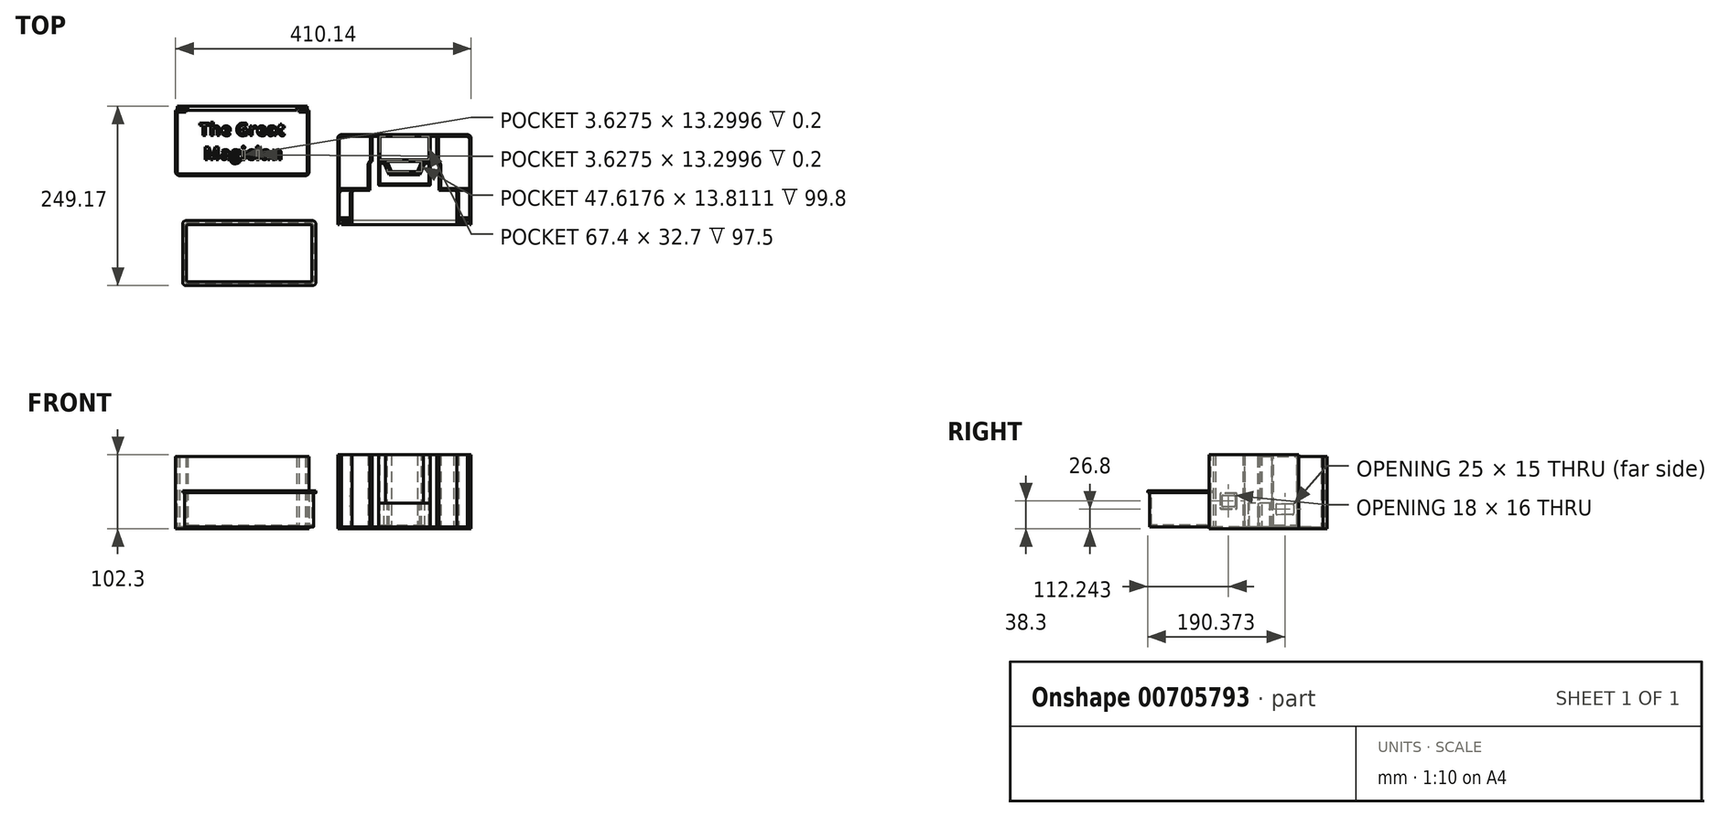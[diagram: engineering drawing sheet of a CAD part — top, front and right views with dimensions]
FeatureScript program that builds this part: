
annotation { "Feature Type Name" : "Feature", "Feature Type Description" : "" }
export const myFeature = defineFeature(function(context is Context, id is Id, definition is map)
    precondition{}
    {
        {
            var Q0;
            Q0=qCreatedBy(makeId("Top.planeOp"),FACE);
            var sketch = newSketch(context, id + "F0", { "sketchPlane" : qUnion([Q0])});
            skLineSegment(sketch, "E0.top", {"start": v(-1, -57.37) * mm, "end": v(-73, -57.37) * mm});
            skLineSegment(sketch, "E0.right", {"start": v(-73, -12.37) * mm, "end": v(-73, -57.37) * mm});
            skLineSegment(sketch, "E1.right", {"start": v(-84, -57.37) * mm, "end": v(-84, -57.37) * mm});
            skLineSegment(sketch, "E2.top", {"start": v(0, 62.63) * mm, "end": v(-45, 62.63) * mm});
            skLineSegment(sketch, "E2.right", {"start": v(-45, 27.63) * mm, "end": v(-45, 62.63) * mm});
            skLineSegment(sketch, "E3.MirrorCS", {"start": v(45, 27.63) * mm, "end": v(45, 62.63) * mm});
            skLineSegment(sketch, "E4.MirrorCS", {"start": v(0, 62.63) * mm, "end": v(45, 62.63) * mm});
            skLineSegment(sketch, "E5.MirrorCS", {"start": v(73, -12.37) * mm, "end": v(73, -57.37) * mm});
            skLineSegment(sketch, "E6.MirrorCS", {"start": v(-1, -57.37) * mm, "end": v(73, -57.37) * mm});
            skLineSegment(sketch, "E7", {"start": v(-36, 62.63) * mm, "end": v(-36, 27.63) * mm});
            skLineSegment(sketch, "E8.MirrorCS", {"start": v(36, 73.63) * mm, "end": v(36, 27.63) * mm});
            skLineSegment(sketch, "E9.trimOffspring", {"start": v(-48, -12.37) * mm, "end": v(-73, -12.37) * mm});
            skPoint(sketch, "E10.orphan", {"position": v(40, -12.37) * mm});
            skLineSegment(sketch, "E11.trimOffspring", {"start": v(48, -12.37) * mm, "end": v(73, -12.37) * mm});
            skPoint(sketch, "E12.orphan", {"position": v(73, -57.37) * mm});
            skPoint(sketch, "E13.orphan", {"position": v(0, 62.63) * mm});
            skLineSegment(sketch, "E14.bottom", {"start": v(-304.84, -57.37) * mm, "end": v(-125.84, -57.37) * mm});
            skLineSegment(sketch, "E14.top", {"start": v(-304.84, -141.67) * mm, "end": v(-125.84, -141.67) * mm});
            skLineSegment(sketch, "E14.left", {"start": v(-304.84, -57.37) * mm, "end": v(-304.84, -141.67) * mm});
            skLineSegment(sketch, "E14.right", {"start": v(-125.84, -57.37) * mm, "end": v(-125.84, -141.67) * mm});
            skLineSegment(sketch, "E15.0", {"start": v(-307.84, -54.37) * mm, "end": v(-122.84, -54.37) * mm});
            skLineSegment(sketch, "E15.1", {"start": v(-307.84, -54.37) * mm, "end": v(-307.84, -144.67) * mm});
            skLineSegment(sketch, "E15.2", {"start": v(-307.84, -144.67) * mm, "end": v(-122.84, -144.67) * mm});
            skLineSegment(sketch, "E15.3", {"start": v(-122.84, -54.37) * mm, "end": v(-122.84, -144.67) * mm});
            skLineSegment(sketch, "E16", {"start": v(-36, 27.63) * mm, "end": v(36, 27.63) * mm});
            skLineSegment(sketch, "E17", {"start": v(-45, 27.63) * mm, "end": v(-48, 27.63) * mm});
            skLineSegment(sketch, "E18", {"start": v(-48, 27.63) * mm, "end": v(-48, -12.37) * mm});
            skLineSegment(sketch, "E19", {"start": v(0, 62.63) * mm, "end": v(0, 0) * mm, "construction": true});
            skLineSegment(sketch, "E20.MirrorCS", {"start": v(45, 27.63) * mm, "end": v(48, 27.63) * mm});
            skLineSegment(sketch, "E21.MirrorCS", {"start": v(48, 27.63) * mm, "end": v(48, -12.37) * mm});
            skLineSegment(sketch, "E22", {"start": v(-36, 27.63) * mm, "end": v(-26.5, 27.63) * mm});
            skLineSegment(sketch, "E23", {"start": v(-26.5, 27.63) * mm, "end": v(-20, 11.32) * mm});
            skLineSegment(sketch, "E24", {"start": v(-20, 11.32) * mm, "end": v(0, 11.32) * mm});
            skLineSegment(sketch, "E25.MirrorCS", {"start": v(20, 11.32) * mm, "end": v(0, 11.32) * mm});
            skLineSegment(sketch, "E26.MirrorCS", {"start": v(26.5, 27.63) * mm, "end": v(20, 11.32) * mm});
            skLineSegment(sketch, "E27.MirrorCS", {"start": v(36, 27.63) * mm, "end": v(26.5, 27.63) * mm});
            skPoint(sketch, "E28.MirrorCS.end.orphan", {"position": v(36, -18.37) * mm});
            skPoint(sketch, "E0.bottom.end.orphan", {"position": v(-36, -7.37) * mm});
            skLineSegment(sketch, "E29", {"start": v(-36, 27.63) * mm, "end": v(-36, -5.6) * mm});
            skLineSegment(sketch, "E30", {"start": v(-36, -5.6) * mm, "end": v(36, -5.6) * mm});
            skLineSegment(sketch, "E31", {"start": v(36, 27.63) * mm, "end": v(36, -5.6) * mm});
            skLineSegment(sketch, "E32.top", {"start": v(-303.24, 96.2) * mm, "end": v(-315.24, 96.2) * mm});
            skLineSegment(sketch, "E32.right", {"start": v(-315.24, 10.5) * mm, "end": v(-315.24, 96.2) * mm});
            skLineSegment(sketch, "E33.MirrorCS", {"start": v(-134.64, 10.5) * mm, "end": v(-134.64, 96.2) * mm});
            skPoint(sketch, "E34.MirrorCS.end.orphan", {"position": v(84, -57.37) * mm});
            skPoint(sketch, "E35.MirrorCS.end.orphan", {"position": v(84, -57.73) * mm});
            skLineSegment(sketch, "E36.1", {"start": v(-132.34, 8.2) * mm, "end": v(-132.34, 98.5) * mm});
            skLineSegment(sketch, "E36.4", {"start": v(-303.24, 98.5) * mm, "end": v(-312.34, 98.5) * mm});
            skLineSegment(sketch, "E36.5", {"start": v(-317.54, 8.2) * mm, "end": v(-317.54, 98.5) * mm});
            skLineSegment(sketch, "E37", {"start": v(-303.24, 96.2) * mm, "end": v(-303.24, 98.5) * mm});
            skLineSegment(sketch, "E38.top", {"start": v(-315.04, 104.5) * mm, "end": v(-312.34, 104.5) * mm});
            skLineSegment(sketch, "E38.right", {"start": v(-312.34, 98.5) * mm, "end": v(-312.34, 101.8) * mm});
            skLineSegment(sketch, "E39.bottom", {"start": v(-312.34, 104.5) * mm, "end": v(-300.54, 104.5) * mm});
            skLineSegment(sketch, "E39.top", {"start": v(-312.34, 101.8) * mm, "end": v(-300.54, 101.8) * mm});
            skLineSegment(sketch, "E39.right", {"start": v(-300.54, 104.5) * mm, "end": v(-300.54, 101.8) * mm});
            skLineSegment(sketch, "E40.trimOffspring", {"start": v(-315.24, 98.5) * mm, "end": v(-317.54, 98.5) * mm});
            skLineSegment(sketch, "E41", {"start": v(-315.24, 10.5) * mm, "end": v(-134.64, 10.5) * mm});
            skLineSegment(sketch, "E42", {"start": v(-317.54, 8.2) * mm, "end": v(-132.34, 8.2) * mm});
            skLineSegment(sketch, "E43", {"start": v(-224.94, 10.5) * mm, "end": v(-224.94, 18.93) * mm, "construction": true});
            skLineSegment(sketch, "E44.MirrorCS", {"start": v(-137.54, 98.5) * mm, "end": v(-137.54, 101.8) * mm});
            skLineSegment(sketch, "E45.MirrorCS", {"start": v(-137.54, 104.5) * mm, "end": v(-149.34, 104.5) * mm});
            skLineSegment(sketch, "E46.MirrorCS", {"start": v(-137.54, 101.8) * mm, "end": v(-149.34, 101.8) * mm});
            skLineSegment(sketch, "E47.MirrorCS", {"start": v(-149.34, 104.5) * mm, "end": v(-149.34, 101.8) * mm});
            skLineSegment(sketch, "E48.MirrorCS", {"start": v(-146.64, 98.5) * mm, "end": v(-137.54, 98.5) * mm});
            skLineSegment(sketch, "E49.MirrorCS", {"start": v(-146.64, 96.2) * mm, "end": v(-146.64, 98.5) * mm});
            skLineSegment(sketch, "E50.MirrorCS", {"start": v(-146.64, 96.2) * mm, "end": v(-134.64, 96.2) * mm});
            skLineSegment(sketch, "E51.MirrorCS", {"start": v(-134.64, 98.5) * mm, "end": v(-132.34, 98.5) * mm});
            skLineSegment(sketch, "E52", {"start": v(-315.24, 98.5) * mm, "end": v(-315.04, 98.5) * mm});
            skLineSegment(sketch, "E53", {"start": v(-315.04, 98.5) * mm, "end": v(-315.04, 104.5) * mm});
            skPoint(sketch, "E54.orphan", {"position": v(-315.24, 104.5) * mm});
            skLineSegment(sketch, "E55.MirrorCS", {"start": v(-134.84, 98.5) * mm, "end": v(-134.84, 104.5) * mm});
            skLineSegment(sketch, "E56.MirrorCS", {"start": v(-134.84, 104.5) * mm, "end": v(-137.54, 104.5) * mm});
            skLineSegment(sketch, "E57.MirrorCS", {"start": v(-134.64, 98.5) * mm, "end": v(-134.84, 98.5) * mm});
            skSolve(sketch);
        }
        {
            var Q0;
            Q0=makeQuery(id+"F0.imprint","IMPRINT",FACE,{"disambiguationData":[TD([[makeQuery(id+"F0.imprint","IMPRINT",EDGE,{"derivedFrom":sQuery(id+"F0.wireOp",EDGE,"E0.top")}),-1.0]])]});
            var Q1;
            {var subQ4=sQuery(id+"F0.wireOp",EDGE,"E0.left");Q1=makeQuery(id+"F0.imprint","IMPRINT",FACE,{"disambiguationData":[TD([[makeQuery(id+"F0.imprint","IMPRINT",EDGE,{"derivedFrom":subQ4}),1.0]])]});}
            var Q2;
            Q2=makeQuery(id+"F0.imprint","IMPRINT",FACE,{"disambiguationData":[TD([[makeQuery(id+"F0.imprint","IMPRINT",EDGE,{"derivedFrom":sQuery(id+"F0.wireOp",EDGE,"E0.bottom")}),1.0]])]});
            var Q3;
            Q3=makeQuery(id+"F0.imprint","IMPRINT",FACE,{"disambiguationData":[TD([[makeQuery(id+"F0.imprint","IMPRINT",EDGE,{"derivedFrom":sQuery(id+"F0.wireOp",EDGE,"E1.bottom")}),-1.0]])]});
            var Q4;
            {var subQ2=sQuery(id+"F0.wireOp",EDGE,"E35.MirrorCS");Q4=makeQuery(id+"F0.imprint","IMPRINT",FACE,{"disambiguationData":[TD([[makeQuery(id+"F0.imprint","IMPRINT",EDGE,{"derivedFrom":subQ2}),-1.0]])]});}
            var Q5;
            Q5=makeQuery(id+"F0.imprint","IMPRINT",FACE,{"disambiguationData":[TD([[makeQuery(id+"F0.imprint","IMPRINT",EDGE,{"derivedFrom":sQuery(id+"F0.wireOp",EDGE,"E2.bottom")}),-1.0]])]});
            var Q6;
            {var subQ0=sQuery(id+"F0.wireOp",EDGE,"E7");Q6=makeQuery(id+"F0.imprint","IMPRINT",FACE,{"disambiguationData":[TD([[makeQuery(id+"F0.imprint","IMPRINT",EDGE,{"derivedFrom":subQ0}),1.0]])]});}
            var Q7;
            {var subQ0=sQuery(id+"F0.wireOp",EDGE,"E23");Q7=makeQuery(id+"F0.imprint","IMPRINT",FACE,{"disambiguationData":[TD([[makeQuery(id+"F0.imprint","IMPRINT",EDGE,{"derivedFrom":subQ0}),1.0]])]});}
            var Q8;
            {var subQ0=sQuery(id+"F0.wireOp",EDGE,"E23");Q8=makeQuery(id+"F0.imprint","IMPRINT",FACE,{"disambiguationData":[TD([[makeQuery(id+"F0.imprint","IMPRINT",EDGE,{"derivedFrom":subQ0}),-1.0]])]});}
            var Q9;
            Q9=makeQuery(id+"F0.imprint","IMPRINT",FACE,{"disambiguationData":[TD([[makeQuery(id+"F0.imprint","IMPRINT",EDGE,{"derivedFrom":sQuery(id+"F0.wireOp",EDGE,"c8318e10-518c-48d9-a7b7-4d28b4569db7.top")}),1.0]])]});
            extrude(context, id + "F1", {"entities" : qUnion([Q0, Q1, Q2, Q3, Q4, Q5, Q6, Q7, Q8, Q9]), "depth" : 100 * mm, "offsetDistance" : 25 * mm});
        }
        {
            var Q0;
            Q0=makeQuery(id+"F0.imprint","IMPRINT",FACE,{"disambiguationData":[TD([[makeQuery(id+"F0.imprint","IMPRINT",EDGE,{"derivedFrom":sQuery(id+"F0.wireOp",EDGE,"E32.top")}),-1.0]])]});
            extrude(context, id + "F2", {"entities" : qUnion([Q0]), "depth" : 97.5 * mm, "offsetDistance" : 25 * mm});
        }
        {
            var Q0;
            Q0=makeQuery(id+"F1.opExtrude","SWEPT_EDGE",EDGE,{"disambiguationData":[OSD([sQuery(id+"F0.wireOp",EDGE,"E0.right"),sQuery(id+"F0.wireOp",EDGE,"E9.trimOffspring")])]});
            var Q1;
            Q1=makeQuery(id+"F1.opExtrude","SWEPT_EDGE",EDGE,{"disambiguationData":[OSD([sQuery(id+"F0.wireOp",EDGE,"E17"),sQuery(id+"F0.wireOp",EDGE,"E18")])]});
            var Q2;
            Q2=makeQuery(id+"F1.opExtrude","SWEPT_EDGE",EDGE,{"disambiguationData":[OSD([sQuery(id+"F0.wireOp",EDGE,"E20.MirrorCS"),sQuery(id+"F0.wireOp",EDGE,"E21.MirrorCS")])]});
            var Q3;
            Q3=makeQuery(id+"F1.opExtrude","SWEPT_EDGE",EDGE,{"disambiguationData":[OSD([sQuery(id+"F0.wireOp",EDGE,"E5.MirrorCS"),sQuery(id+"F0.wireOp",EDGE,"E11.trimOffspring")])]});
            fillet(context, id + "F3", {"entities" : qUnion([Q0, Q1, Q2, Q3]), "radius" : 5 * mm, "tangentPropagation" : true, "allowEdgeOverflow" : false});
        }
        {
            var Q0;
            Q0=makeQuery(id+"F1.opExtrude","CAP_FACE",FACE,{"disambiguationData":[OSD([sQuery(id+"F0.wireOp",EDGE,"E0.top"),sQuery(id+"F0.wireOp",EDGE,"E0.right"),sQuery(id+"F0.wireOp",EDGE,"E2.top"),sQuery(id+"F0.wireOp",EDGE,"E2.right"),sQuery(id+"F0.wireOp",EDGE,"E3.MirrorCS"),sQuery(id+"F0.wireOp",EDGE,"E4.MirrorCS"),sQuery(id+"F0.wireOp",EDGE,"E5.MirrorCS"),sQuery(id+"F0.wireOp",EDGE,"E6.MirrorCS"),sQuery(id+"F0.wireOp",EDGE,"E9.trimOffspring"),sQuery(id+"F0.wireOp",EDGE,"E11.trimOffspring"),sQuery(id+"F0.wireOp",EDGE,"E17"),sQuery(id+"F0.wireOp",EDGE,"E18"),sQuery(id+"F0.wireOp",EDGE,"E20.MirrorCS"),sQuery(id+"F0.wireOp",EDGE,"E21.MirrorCS")])],"isStart":false});
            shell(context, id + "F4", {"entities" : qUnion([Q0]), "thickness" : 2.3 * mm, "oppositeDirection" : true});
        }
        {
            var Q0;
            {var subQ0=sQuery(id+"F0.wireOp",EDGE,"E7");Q0=makeQuery(id+"F0.imprint","IMPRINT",FACE,{"disambiguationData":[TD([[makeQuery(id+"F0.imprint","IMPRINT",EDGE,{"derivedFrom":subQ0}),1.0]])]});}
            var Q1;
            {var subQ4=sQuery(id+"F0.wireOp",EDGE,"E2.bottom");Q1=makeQuery(id+"F0.imprint","IMPRINT",FACE,{"disambiguationData":[TD([[makeQuery(id+"F0.imprint","IMPRINT",EDGE,{"derivedFrom":subQ4}),-1.0]])]});}
            var Q2;
            {var subQ0=sQuery(id+"F0.wireOp",EDGE,"E23");Q2=makeQuery(id+"F0.imprint","IMPRINT",FACE,{"disambiguationData":[TD([[makeQuery(id+"F0.imprint","IMPRINT",EDGE,{"derivedFrom":subQ0}),1.0]])]});}
            extrude(context, id + "F5", {"entities" : qUnion([Q0, Q1, Q2]), "operationType" : NewBodyOperationType.ADD, "depth" : 100 * mm, "offsetDistance" : 25 * mm});
        }
        {
            var Q0;
            {var subQ0=sQuery(id+"F0.wireOp",EDGE,"E4.MirrorCS");var subQ1=sQuery(id+"F0.wireOp",EDGE,"E2.top");Q0=makeQuery(id+"F5.boolean.opBoolean","MERGE",FACE,{"derivedFrom":[makeQuery(id+"F1.opExtrude","CAP_FACE",FACE,{"disambiguationData":[OSD([sQuery(id+"F0.wireOp",EDGE,"E0.top"),sQuery(id+"F0.wireOp",EDGE,"E0.right"),subQ1,sQuery(id+"F0.wireOp",EDGE,"E2.right"),sQuery(id+"F0.wireOp",EDGE,"E3.MirrorCS"),subQ0,sQuery(id+"F0.wireOp",EDGE,"E5.MirrorCS"),sQuery(id+"F0.wireOp",EDGE,"E6.MirrorCS"),sQuery(id+"F0.wireOp",EDGE,"E9.trimOffspring"),sQuery(id+"F0.wireOp",EDGE,"E11.trimOffspring"),sQuery(id+"F0.wireOp",EDGE,"E17"),sQuery(id+"F0.wireOp",EDGE,"E18"),sQuery(id+"F0.wireOp",EDGE,"E20.MirrorCS"),sQuery(id+"F0.wireOp",EDGE,"E21.MirrorCS")])],"isStart":false}),makeQuery(id+"F5.opExtrude","CAP_FACE",FACE,{"disambiguationData":[OSD([subQ1,subQ0,sQuery(id+"F0.wireOp",EDGE,"E7"),sQuery(id+"F0.wireOp",EDGE,"E8.MirrorCS"),sQuery(id+"F0.wireOp",EDGE,"E16"),sQuery(id+"F0.wireOp",EDGE,"E23"),sQuery(id+"F0.wireOp",EDGE,"E24"),sQuery(id+"F0.wireOp",EDGE,"E25.MirrorCS"),sQuery(id+"F0.wireOp",EDGE,"E26.MirrorCS")])],"isStart":false})]});}
            shell(context, id + "F6", {"entities" : qUnion([Q0]), "thickness" : 2.5 * mm});
        }
        {
            var Q0;
            {var subQ0=sQuery(id+"F0.wireOp",EDGE,"E23");Q0=makeQuery(id+"F0.imprint","IMPRINT",FACE,{"disambiguationData":[TD([[makeQuery(id+"F0.imprint","IMPRINT",EDGE,{"derivedFrom":subQ0}),-1.0]])]});}
            extrude(context, id + "F7", {"entities" : qUnion([Q0]), "operationType" : NewBodyOperationType.ADD, "depth" : 33 * mm, "offsetDistance" : 25 * mm});
        }
        {
            var Q0;
            Q0=makeQuery(id+"F0.imprint","IMPRINT",FACE,{"disambiguationData":[TD([[makeQuery(id+"F0.imprint","IMPRINT",EDGE,{"derivedFrom":sQuery(id+"F0.wireOp",EDGE,"E14.bottom")}),-1.0]])]});
            var Q1;
            Q1=makeQuery(id+"F0.imprint","IMPRINT",FACE,{"disambiguationData":[TD([[makeQuery(id+"F0.imprint","IMPRINT",EDGE,{"derivedFrom":sQuery(id+"F0.wireOp",EDGE,"E14.bottom")}),1.0]])]});
            extrude(context, id + "F8", {"entities" : qUnion([Q0, Q1]), "depth" : 50 * mm, "offsetDistance" : 25 * mm});
        }
        {
            var Q0;
            Q0=makeQuery(id+"F0.imprint","IMPRINT",FACE,{"disambiguationData":[TD([[makeQuery(id+"F0.imprint","IMPRINT",EDGE,{"derivedFrom":sQuery(id+"F0.wireOp",EDGE,"E14.bottom")}),1.0]])]});
            extrude(context, id + "F9", {"entities" : qUnion([Q0]), "operationType" : NewBodyOperationType.REMOVE, "depth" : 47.5 * mm, "offsetDistance" : 25 * mm});
        }
        {
            var Q0;
            Q0=makeQuery(id+"F9.boolean.opBoolean","COPY",EDGE,{"derivedFrom":makeQuery(id+"F9.opExtrude","SWEPT_EDGE",EDGE,{"disambiguationData":[OSD([sQuery(id+"F0.wireOp",EDGE,"E14.top"),sQuery(id+"F0.wireOp",EDGE,"E14.left")])]})});
            var Q1;
            Q1=makeQuery(id+"F9.boolean.opBoolean","COPY",EDGE,{"derivedFrom":makeQuery(id+"F9.opExtrude","SWEPT_EDGE",EDGE,{"disambiguationData":[OSD([sQuery(id+"F0.wireOp",EDGE,"E14.bottom"),sQuery(id+"F0.wireOp",EDGE,"E14.left")])]})});
            var Q2;
            Q2=makeQuery(id+"F8.opExtrude","SWEPT_EDGE",EDGE,{"disambiguationData":[OSD([sQuery(id+"F0.wireOp",EDGE,"E15.1"),sQuery(id+"F0.wireOp",EDGE,"E15.2")])]});
            var Q3;
            Q3=makeQuery(id+"F8.opExtrude","SWEPT_EDGE",EDGE,{"disambiguationData":[OSD([sQuery(id+"F0.wireOp",EDGE,"E15.0"),sQuery(id+"F0.wireOp",EDGE,"E15.1")])]});
            var Q4;
            Q4=makeQuery(id+"F8.opExtrude","SWEPT_EDGE",EDGE,{"disambiguationData":[OSD([sQuery(id+"F0.wireOp",EDGE,"E15.0"),sQuery(id+"F0.wireOp",EDGE,"E15.3")])]});
            var Q5;
            Q5=makeQuery(id+"F9.boolean.opBoolean","COPY",EDGE,{"derivedFrom":makeQuery(id+"F9.opExtrude","SWEPT_EDGE",EDGE,{"disambiguationData":[OSD([sQuery(id+"F0.wireOp",EDGE,"E14.bottom"),sQuery(id+"F0.wireOp",EDGE,"E14.right")])]})});
            var Q6;
            Q6=makeQuery(id+"F8.opExtrude","SWEPT_EDGE",EDGE,{"disambiguationData":[OSD([sQuery(id+"F0.wireOp",EDGE,"E15.2"),sQuery(id+"F0.wireOp",EDGE,"E15.3")])]});
            var Q7;
            Q7=makeQuery(id+"F9.boolean.opBoolean","COPY",EDGE,{"derivedFrom":makeQuery(id+"F9.opExtrude","SWEPT_EDGE",EDGE,{"disambiguationData":[OSD([sQuery(id+"F0.wireOp",EDGE,"E14.top"),sQuery(id+"F0.wireOp",EDGE,"E14.right")])]})});
            fillet(context, id + "F10", {"entities" : qUnion([Q0, Q1, Q2, Q3, Q4, Q5, Q6, Q7]), "radius" : 5 * mm, "tangentPropagation" : true, "allowEdgeOverflow" : false});
        }
        {
            var Q0;
            Q0=makeQuery(id+"F8.opExtrude","CAP_FACE",FACE,{"disambiguationData":[OSD([sQuery(id+"F0.wireOp",EDGE,"E15.0"),sQuery(id+"F0.wireOp",EDGE,"E15.1"),sQuery(id+"F0.wireOp",EDGE,"E15.2"),sQuery(id+"F0.wireOp",EDGE,"E15.3")])],"isStart":false});
            shell(context, id + "F11", {"entities" : qUnion([Q0]), "thickness" : 2.5 * mm});
        }
        {
            var Q0;
            Q0=makeQuery(id+"F1.opExtrude","SWEPT_EDGE",EDGE,{"disambiguationData":[OSD([sQuery(id+"F0.wireOp",EDGE,"E0.top"),sQuery(id+"F0.wireOp",EDGE,"E0.right")])]});
            var Q1;
            Q1=makeQuery(id+"F1.opExtrude","SWEPT_EDGE",EDGE,{"disambiguationData":[OSD([sQuery(id+"F0.wireOp",EDGE,"E5.MirrorCS"),sQuery(id+"F0.wireOp",EDGE,"E6.MirrorCS")])]});
            var Q2;
            Q2=makeQuery(id+"F1.opExtrude","SWEPT_EDGE",EDGE,{"disambiguationData":[OSD([sQuery(id+"F0.wireOp",EDGE,"E9.trimOffspring"),sQuery(id+"F0.wireOp",EDGE,"E18")])]});
            var Q3;
            Q3=makeQuery(id+"F1.opExtrude","SWEPT_EDGE",EDGE,{"disambiguationData":[OSD([sQuery(id+"F0.wireOp",EDGE,"E11.trimOffspring"),sQuery(id+"F0.wireOp",EDGE,"E21.MirrorCS")])]});
            fillet(context, id + "F12", {"entities" : qUnion([Q0, Q1, Q2, Q3]), "radius" : 1 * mm, "tangentPropagation" : true, "allowEdgeOverflow" : false});
        }
        {
            var Q0;
            {var subQ0=sQuery(id+"F0.wireOp",EDGE,"E7");Q0=makeQuery(id+"F0.imprint","IMPRINT",FACE,{"disambiguationData":[TD([[makeQuery(id+"F0.imprint","IMPRINT",EDGE,{"derivedFrom":subQ0}),1.0]])]});}
            extrude(context, id + "F13", {"entities" : qUnion([Q0]), "operationType" : NewBodyOperationType.ADD, "depth" : 100 * mm, "offsetDistance" : 25 * mm});
        }
        {
            var Q0;
            {var subQ0=sQuery(id+"F0.wireOp",EDGE,"E16");var subQ1=sQuery(id+"F0.wireOp",EDGE,"E8.MirrorCS");var subQ2=sQuery(id+"F0.wireOp",EDGE,"E7");var subQ3=sQuery(id+"F0.wireOp",EDGE,"E4.MirrorCS");var subQ4=sQuery(id+"F0.wireOp",EDGE,"E2.top");Q0=makeQuery(id+"F13.boolean.opBoolean","MERGE",FACE,{"derivedFrom":[makeQuery(id+"F5.boolean.opBoolean","MERGE",FACE,{"derivedFrom":[makeQuery(id+"F1.opExtrude","CAP_FACE",FACE,{"disambiguationData":[OSD([sQuery(id+"F0.wireOp",EDGE,"E0.top"),sQuery(id+"F0.wireOp",EDGE,"E0.right"),subQ4,sQuery(id+"F0.wireOp",EDGE,"E2.right"),sQuery(id+"F0.wireOp",EDGE,"E3.MirrorCS"),subQ3,sQuery(id+"F0.wireOp",EDGE,"E5.MirrorCS"),sQuery(id+"F0.wireOp",EDGE,"E6.MirrorCS"),sQuery(id+"F0.wireOp",EDGE,"E9.trimOffspring"),sQuery(id+"F0.wireOp",EDGE,"E11.trimOffspring"),sQuery(id+"F0.wireOp",EDGE,"E17"),sQuery(id+"F0.wireOp",EDGE,"E18"),sQuery(id+"F0.wireOp",EDGE,"E20.MirrorCS"),sQuery(id+"F0.wireOp",EDGE,"E21.MirrorCS")])],"isStart":false}),makeQuery(id+"F5.opExtrude","CAP_FACE",FACE,{"disambiguationData":[OSD([subQ4,subQ3,subQ2,subQ1,subQ0,sQuery(id+"F0.wireOp",EDGE,"E23"),sQuery(id+"F0.wireOp",EDGE,"E24"),sQuery(id+"F0.wireOp",EDGE,"E25.MirrorCS"),sQuery(id+"F0.wireOp",EDGE,"E26.MirrorCS")])],"isStart":false})]}),makeQuery(id+"F13.opExtrude","CAP_FACE",FACE,{"disambiguationData":[OSD([subQ4,subQ3,subQ2,subQ1,subQ0])],"isStart":false})]});}
            var sketch = newSketch(context, id + "F14", { "sketchPlane" : qUnion([Q0])});
            skPoint(sketch, "E58.oppositeSnap0", {"position": v(40.5, 62.63) * mm});
            skLineSegment(sketch, "E59.bottom", {"start": v(-33.7, 29.93) * mm, "end": v(33.7, 29.93) * mm});
            skLineSegment(sketch, "E59.top", {"start": v(-33.7, 62.63) * mm, "end": v(33.7, 62.63) * mm});
            skLineSegment(sketch, "E59.left", {"start": v(-33.7, 29.93) * mm, "end": v(-33.7, 62.63) * mm});
            skLineSegment(sketch, "E59.right", {"start": v(33.7, 29.93) * mm, "end": v(33.7, 62.63) * mm});
            skSolve(sketch);
        }
        {
            var Q0;
            Q0=makeQuery(id+"F14.imprint","IMPRINT",FACE,{"disambiguationData":[TD([[makeQuery(id+"F14.imprint","IMPRINT",EDGE,{"derivedFrom":sQuery(id+"F14.wireOp",EDGE,"E59.bottom")}),1.0]])]});
            extrude(context, id + "F15", {"entities" : qUnion([Q0]), "operationType" : NewBodyOperationType.REMOVE, "oppositeDirection" : true, "depth" : 97.5 * mm, "offsetDistance" : 25 * mm});
        }
        {
            var Q0;
            Q0=makeQuery(id+"F14.imprint","IMPRINT",FACE,{"disambiguationData":[TD([[makeQuery(id+"F14.imprint","IMPRINT",EDGE,{"derivedFrom":sQuery(id+"F14.wireOp",EDGE,"E59.bottom")}),-1.0]])]});
            var sketch = newSketch(context, id + "F16", { "sketchPlane" : qUnion([Q0])});
            skLineSegment(sketch, "E60.bottom", {"start": v(-73, -57.37) * mm, "end": v(73, -57.37) * mm});
            skLineSegment(sketch, "E60.top", {"start": v(-73, -59.67) * mm, "end": v(73, -59.67) * mm});
            skLineSegment(sketch, "E60.left", {"start": v(-73, -57.37) * mm, "end": v(-73, -59.67) * mm});
            skLineSegment(sketch, "E60.right", {"start": v(73, -57.37) * mm, "end": v(73, -59.67) * mm});
            skLineSegment(sketch, "E61.bottom", {"start": v(-72.99, -56.77) * mm, "end": v(-87.2, -56.77) * mm});
            skLineSegment(sketch, "E61.top", {"start": v(-72, -59.67) * mm, "end": v(-87.2, -59.67) * mm});
            skLineSegment(sketch, "E61.right", {"start": v(-87.2, -56.77) * mm, "end": v(-87.2, -59.67) * mm});
            skLineSegment(sketch, "E62.top", {"start": v(74, -59.67) * mm, "end": v(87.2, -59.67) * mm});
            skPoint(sketch, "E63", {"position": v(-72.99, -56.77) * mm});
            skLineSegment(sketch, "E64", {"start": v(0, -57.37) * mm, "end": v(0, -53.18) * mm, "construction": true});
            skLineSegment(sketch, "E65.MirrorCS", {"start": v(72.99, -56.77) * mm, "end": v(87.2, -56.77) * mm});
            skLineSegment(sketch, "E66.MirrorCS", {"start": v(87.2, -56.77) * mm, "end": v(87.2, -59.67) * mm});
            skLineSegment(sketch, "E67.MirrorCS", {"start": v(72, -59.67) * mm, "end": v(87.2, -59.67) * mm});
            skSolve(sketch);
        }
        {
            var Q0;
            Q0=makeQuery(id+"F16.imprint","IMPRINT",FACE,{"disambiguationData":[TD([[makeQuery(id+"F16.imprint","IMPRINT",EDGE,{"derivedFrom":sQuery(id+"F16.wireOp",EDGE,"E60.bottom")}),1.0]])]});
            extrude(context, id + "F17", {"entities" : qUnion([Q0]), "operationType" : NewBodyOperationType.REMOVE, "oppositeDirection" : true, "depth" : 100 * mm, "offsetDistance" : 25 * mm});
        }
        {
            var Q0;
            {var subQ0=sQuery(id+"F16.wireOp",EDGE,"E61.right");Q0=makeQuery(id+"F16.imprint","IMPRINT",FACE,{"disambiguationData":[TD([[makeQuery(id+"F16.imprint","IMPRINT",EDGE,{"derivedFrom":subQ0}),1.0]])]});}
            var Q1;
            {var subQ0=sQuery(id+"F16.wireOp",EDGE,"E62.right");Q1=makeQuery(id+"F16.imprint","IMPRINT",FACE,{"disambiguationData":[TD([[makeQuery(id+"F16.imprint","IMPRINT",EDGE,{"derivedFrom":subQ0}),-1.0]])]});}
            var Q2;
            {var subQ6=sQuery(id+"F16.wireOp",EDGE,"E66.MirrorCS");Q2=makeQuery(id+"F16.imprint","IMPRINT",FACE,{"disambiguationData":[TD([[makeQuery(id+"F16.imprint","IMPRINT",EDGE,{"derivedFrom":subQ6}),-1.0]])]});}
            extrude(context, id + "F18", {"entities" : qUnion([Q0, Q1, Q2]), "operationType" : NewBodyOperationType.ADD, "oppositeDirection" : true, "depth" : 100 * mm, "offsetDistance" : 25 * mm});
        }
        {
            var Q0;
            Q0=makeQuery(id+"F2.opExtrude","SWEPT_FACE",FACE,{"disambiguationData":[OSD([sQuery(id+"F0.wireOp",EDGE,"E36.5")])]});
            var sketch = newSketch(context, id + "F19", { "sketchPlane" : qUnion([Q0])});
            skLineSegment(sketch, "E68.bottom", {"start": v(-58.2, 32) * mm, "end": v(-33.2, 32) * mm});
            skLineSegment(sketch, "E68.top", {"start": v(-58.2, 17) * mm, "end": v(-33.2, 17) * mm});
            skLineSegment(sketch, "E68.left", {"start": v(-58.2, 32) * mm, "end": v(-58.2, 17) * mm});
            skLineSegment(sketch, "E68.right", {"start": v(-33.2, 32) * mm, "end": v(-33.2, 17) * mm});
            skSolve(sketch);
        }
        {
            var Q0;
            Q0=makeQuery(id+"F1.opExtrude","SWEPT_FACE",FACE,{"disambiguationData":[OSD([sQuery(id+"F0.wireOp",EDGE,"E0.right")])]});
            var sketch = newSketch(context, id + "F20", { "sketchPlane" : qUnion([Q0])});
            skLineSegment(sketch, "E69.bottom", {"start": v(23.43, 44) * mm, "end": v(41.43, 44) * mm});
            skLineSegment(sketch, "E69.top", {"start": v(23.43, 28) * mm, "end": v(41.43, 28) * mm});
            skLineSegment(sketch, "E69.left", {"start": v(23.43, 44) * mm, "end": v(23.43, 28) * mm});
            skLineSegment(sketch, "E69.right", {"start": v(41.43, 44) * mm, "end": v(41.43, 28) * mm});
            skLineSegment(sketch, "E70", {"start": v(41.43, 28) * mm, "end": v(41.43, 0) * mm, "construction": true});
            skSolve(sketch);
        }
        {
            var Q0;
            Q0=makeQuery(id+"F5.opExtrude","SWEPT_EDGE",EDGE,{"disambiguationData":[OSD([sQuery(id+"F0.wireOp",EDGE,"E7"),sQuery(id+"F0.wireOp",EDGE,"E16"),sQuery(id+"F0.wireOp",EDGE,"E29")])]});
            var Q1;
            Q1=makeQuery(id+"F4.opShell","OFFSET_EDGE",EDGE,{"disambiguationData":[OSD([sQuery(id+"F0.wireOp",EDGE,"E3.MirrorCS"),sQuery(id+"F0.wireOp",EDGE,"E20.MirrorCS"),sQuery(id+"F0.wireOp",EDGE,"E21.MirrorCS")])]});
            var Q2;
            Q2=makeQuery(id+"F5.opExtrude","SWEPT_EDGE",EDGE,{"disambiguationData":[OSD([sQuery(id+"F0.wireOp",EDGE,"E8.MirrorCS"),sQuery(id+"F0.wireOp",EDGE,"E16"),sQuery(id+"F0.wireOp",EDGE,"E31")])]});
            var Q3;
            Q3=makeQuery(id+"F4.opShell","OFFSET_EDGE",EDGE,{"disambiguationData":[OSD([sQuery(id+"F0.wireOp",EDGE,"E2.right"),sQuery(id+"F0.wireOp",EDGE,"E17"),sQuery(id+"F0.wireOp",EDGE,"E18")])]});
            var Q4;
            Q4=makeQuery(id+"F5.opExtrude","SWEPT_EDGE",EDGE,{"disambiguationData":[OSD([sQuery(id+"F0.wireOp",EDGE,"E23"),sQuery(id+"F0.wireOp",EDGE,"E24")])]});
            var Q5;
            Q5=makeQuery(id+"F5.opExtrude","SWEPT_EDGE",EDGE,{"disambiguationData":[OSD([sQuery(id+"F0.wireOp",EDGE,"E25.MirrorCS"),sQuery(id+"F0.wireOp",EDGE,"E26.MirrorCS")])]});
            var Q6;
            Q6=makeQuery(id+"F7.opExtrude","SWEPT_EDGE",EDGE,{"disambiguationData":[OSD([sQuery(id+"F0.wireOp",EDGE,"E30"),sQuery(id+"F0.wireOp",EDGE,"E31")])]});
            var Q7;
            Q7=makeQuery(id+"F7.opExtrude","SWEPT_EDGE",EDGE,{"disambiguationData":[OSD([sQuery(id+"F0.wireOp",EDGE,"E29"),sQuery(id+"F0.wireOp",EDGE,"E30")])]});
            fillet(context, id + "F21", {"entities" : qUnion([Q0, Q1, Q2, Q3, Q4, Q5, Q6, Q7]), "radius" : 1 * mm, "tangentPropagation" : true, "allowEdgeOverflow" : false});
        }
        {
            var Q0;
            Q0=qCreatedBy(makeId("Top.planeOp"),FACE);
            var sketch = newSketch(context, id + "F22", { "sketchPlane" : qUnion([Q0])});
            skLineSegment(sketch, "E71", {"start": v(-47.3, 64.93) * mm, "end": v(-92.6, 64.93) * mm});
            skLineSegment(sketch, "E72", {"start": v(-92.6, 64.93) * mm, "end": v(-92.6, -10.07) * mm});
            skLineSegment(sketch, "E73", {"start": v(-90.3, -10.07) * mm, "end": v(-50.3, -10.07) * mm});
            skLineSegment(sketch, "E74", {"start": v(-50.3, -10.07) * mm, "end": v(-50.3, 29.93) * mm});
            skLineSegment(sketch, "E75", {"start": v(-50.3, 29.93) * mm, "end": v(-47.3, 29.93) * mm});
            skLineSegment(sketch, "E76", {"start": v(-47.3, 29.93) * mm, "end": v(-47.3, 64.93) * mm});
            skLineSegment(sketch, "E77.1", {"start": v(-90.3, 62.63) * mm, "end": v(-90.3, -2.77) * mm});
            skLineSegment(sketch, "E77.3", {"start": v(-46.6, 62.63) * mm, "end": v(-90.3, 62.63) * mm});
            skLineSegment(sketch, "E78", {"start": v(-90.3, -2.77) * mm, "end": v(-90.3, -10.07) * mm});
            skLineSegment(sketch, "E79", {"start": v(-47.3, 62.63) * mm, "end": v(-46.6, 62.63) * mm});
            skLineSegment(sketch, "E80", {"start": v(-92.6, -10.07) * mm, "end": v(-92.6, -12.37) * mm});
            skLineSegment(sketch, "E81", {"start": v(-90.3, -12.37) * mm, "end": v(-75.3, -12.37) * mm});
            skLineSegment(sketch, "E82.MirrorCS", {"start": v(47.3, 64.93) * mm, "end": v(92.6, 64.93) * mm});
            skLineSegment(sketch, "E83.MirrorCS", {"start": v(46.6, 62.63) * mm, "end": v(90.3, 62.63) * mm});
            skLineSegment(sketch, "E84.MirrorCS", {"start": v(47.3, 62.63) * mm, "end": v(46.6, 62.63) * mm});
            skLineSegment(sketch, "E85.MirrorCS", {"start": v(47.3, 29.93) * mm, "end": v(47.3, 64.93) * mm});
            skLineSegment(sketch, "E86.MirrorCS", {"start": v(50.3, 29.93) * mm, "end": v(47.3, 29.93) * mm});
            skLineSegment(sketch, "E87.MirrorCS", {"start": v(50.3, -10.07) * mm, "end": v(50.3, 29.93) * mm});
            skLineSegment(sketch, "E88.MirrorCS", {"start": v(90.3, -10.07) * mm, "end": v(50.3, -10.07) * mm});
            skLineSegment(sketch, "E89.MirrorCS", {"start": v(90.3, -12.37) * mm, "end": v(75.3, -12.37) * mm});
            skLineSegment(sketch, "E90.MirrorCS", {"start": v(90.3, 62.63) * mm, "end": v(90.3, -2.77) * mm});
            skLineSegment(sketch, "E91.MirrorCS", {"start": v(92.6, 64.93) * mm, "end": v(92.6, -10.07) * mm});
            skLineSegment(sketch, "E92.MirrorCS", {"start": v(90.3, -2.77) * mm, "end": v(90.3, -10.07) * mm});
            skPoint(sketch, "E93.orphan", {"position": v(92.6, -10.07) * mm});
            skLineSegment(sketch, "E94.MirrorCS", {"start": v(92.6, -10.07) * mm, "end": v(92.6, -12.37) * mm});
            skLineSegment(sketch, "E95", {"start": v(-92.6, -12.37) * mm, "end": v(-92.6, -59.67) * mm});
            skLineSegment(sketch, "E96", {"start": v(-92.6, -59.67) * mm, "end": v(92.6, -59.67) * mm});
            skLineSegment(sketch, "E97", {"start": v(92.6, -59.67) * mm, "end": v(92.6, -12.37) * mm});
            skLineSegment(sketch, "E98", {"start": v(-90.3, -12.37) * mm, "end": v(-90.3, -57.72) * mm});
            skLineSegment(sketch, "E99", {"start": v(90.3, -57.72) * mm, "end": v(90.3, -12.37) * mm});
            skLineSegment(sketch, "E100", {"start": v(-90.3, -57.72) * mm, "end": v(-90.3, -59.67) * mm});
            skLineSegment(sketch, "E101", {"start": v(90.3, -57.72) * mm, "end": v(90.3, -59.67) * mm});
            skLineSegment(sketch, "E102", {"start": v(-75.3, -12.37) * mm, "end": v(-65.44, -12.37) * mm});
            skLineSegment(sketch, "E103", {"start": v(-65.44, -12.37) * mm, "end": v(-65.44, -10.07) * mm});
            skLineSegment(sketch, "E104", {"start": v(75.3, -12.37) * mm, "end": v(68.1, -12.37) * mm});
            skLineSegment(sketch, "E105", {"start": v(68.1, -12.37) * mm, "end": v(68.1, -10.07) * mm});
            skSolve(sketch);
        }
        {
            var Q0;
            Q0=makeQuery(id+"F22.imprint","IMPRINT",FACE,{"disambiguationData":[TD([[makeQuery(id+"F22.imprint","IMPRINT",EDGE,{"derivedFrom":sQuery(id+"F22.wireOp",EDGE,"E71")}),1.0]])]});
            var Q1;
            {var subQ3=sQuery(id+"F22.wireOp",EDGE,"E80");Q1=makeQuery(id+"F22.imprint","IMPRINT",FACE,{"disambiguationData":[TD([[makeQuery(id+"F22.imprint","IMPRINT",EDGE,{"derivedFrom":subQ3}),1.0]])]});}
            var Q2;
            {var subQ3=sQuery(id+"F22.wireOp",EDGE,"E82.MirrorCS");Q2=makeQuery(id+"F22.imprint","IMPRINT",FACE,{"disambiguationData":[TD([[makeQuery(id+"F22.imprint","IMPRINT",EDGE,{"derivedFrom":subQ3}),-1.0]])]});}
            var Q3;
            Q3=makeQuery(id+"F1.opExtrude","SWEPT_BODY",BODY,{"disambiguationData":[OSD([sQuery(id+"F0.wireOp",EDGE,"E0.top"),sQuery(id+"F0.wireOp",EDGE,"E0.right"),sQuery(id+"F0.wireOp",EDGE,"E2.top"),sQuery(id+"F0.wireOp",EDGE,"E2.right"),sQuery(id+"F0.wireOp",EDGE,"E3.MirrorCS"),sQuery(id+"F0.wireOp",EDGE,"E4.MirrorCS"),sQuery(id+"F0.wireOp",EDGE,"E5.MirrorCS"),sQuery(id+"F0.wireOp",EDGE,"E6.MirrorCS"),sQuery(id+"F0.wireOp",EDGE,"E9.trimOffspring"),sQuery(id+"F0.wireOp",EDGE,"E11.trimOffspring"),sQuery(id+"F0.wireOp",EDGE,"E17"),sQuery(id+"F0.wireOp",EDGE,"E18"),sQuery(id+"F0.wireOp",EDGE,"E20.MirrorCS"),sQuery(id+"F0.wireOp",EDGE,"E21.MirrorCS")])]});
            var Q4;
            Q4=makeQuery(id+"F1.opExtrude","CAP_VERTEX",VERTEX,{"disambiguationData":[OSD([sQuery(id+"F0.wireOp",EDGE,"E2.right"),sQuery(id+"F0.wireOp",EDGE,"E17")])],"isStart":false});
            extrude(context, id + "F23", {"entities" : qUnion([Q0, Q1, Q2]), "operationType" : NewBodyOperationType.ADD, "depth" : 100 * mm, "endBoundEntityBody" : qUnion([Q3]), "endBoundEntityVertex" : qUnion([Q4]), "offsetDistance" : 25 * mm});
        }
        {
            var Q0;
            Q0=makeQuery(id+"F20.imprint","IMPRINT",FACE,{"disambiguationData":[TD([[makeQuery(id+"F20.imprint","IMPRINT",EDGE,{"derivedFrom":sQuery(id+"F20.wireOp",EDGE,"E69.bottom")}),-1.0]])]});
            extrude(context, id + "F24", {"entities" : qUnion([Q0]), "operationType" : NewBodyOperationType.REMOVE, "endBound" : BoundingType.UP_TO_NEXT, "oppositeDirection" : true, "depth" : 25 * mm, "offsetDistance" : 25 * mm, "hasSecondDirection" : true, "secondDirectionOppositeDirection" : false, "secondDirectionDepth" : 25 * mm, "hasSecondDirectionDraft" : true, "secondDirectionDraftAngle" : 10 * degree});
        }
        {
            var Q0;
            Q0=makeQuery(id+"F19.imprint","IMPRINT",FACE,{"disambiguationData":[TD([[makeQuery(id+"F19.imprint","IMPRINT",EDGE,{"derivedFrom":sQuery(id+"F19.wireOp",EDGE,"E68.bottom")}),-1.0]])]});
            extrude(context, id + "F25", {"entities" : qUnion([Q0]), "operationType" : NewBodyOperationType.REMOVE, "endBound" : BoundingType.UP_TO_NEXT, "oppositeDirection" : true, "depth" : 25 * mm, "offsetDistance" : 25 * mm});
        }
        {
            var Q0;
            Q0=makeQuery(id+"F24.boolean.opBoolean","COPY",EDGE,{"derivedFrom":makeQuery(id+"F24.opExtrude","SWEPT_EDGE",EDGE,{"disambiguationData":[OSD([sQuery(id+"F19.wireOp",EDGE,"E68.top"),sQuery(id+"F19.wireOp",EDGE,"E68.right")])]})});
            var Q1;
            Q1=makeQuery(id+"F24.boolean.opBoolean","COPY",EDGE,{"derivedFrom":makeQuery(id+"F24.opExtrude","SWEPT_EDGE",EDGE,{"disambiguationData":[OSD([sQuery(id+"F20.wireOp",EDGE,"E69.top"),sQuery(id+"F20.wireOp",EDGE,"E69.right")])]})});
            var Q2;
            Q2=makeQuery(id+"F24.boolean.opBoolean","COPY",EDGE,{"derivedFrom":makeQuery(id+"F24.opExtrude","SWEPT_EDGE",EDGE,{"disambiguationData":[OSD([sQuery(id+"F20.wireOp",EDGE,"E69.top"),sQuery(id+"F20.wireOp",EDGE,"E69.left")])]})});
            var Q3;
            Q3=makeQuery(id+"F24.boolean.opBoolean","COPY",EDGE,{"derivedFrom":makeQuery(id+"F24.opExtrude","SWEPT_EDGE",EDGE,{"disambiguationData":[OSD([sQuery(id+"F19.wireOp",EDGE,"E68.top"),sQuery(id+"F19.wireOp",EDGE,"E68.left")])]})});
            var Q4;
            Q4=makeQuery(id+"F24.boolean.opBoolean","COPY",EDGE,{"derivedFrom":makeQuery(id+"F24.opExtrude","SWEPT_EDGE",EDGE,{"disambiguationData":[OSD([sQuery(id+"F20.wireOp",EDGE,"E69.bottom"),sQuery(id+"F20.wireOp",EDGE,"E69.left")])]})});
            var Q5;
            Q5=makeQuery(id+"F24.boolean.opBoolean","COPY",EDGE,{"derivedFrom":makeQuery(id+"F24.opExtrude","SWEPT_EDGE",EDGE,{"disambiguationData":[OSD([sQuery(id+"F19.wireOp",EDGE,"E68.bottom"),sQuery(id+"F19.wireOp",EDGE,"E68.left")])]})});
            var Q6;
            Q6=makeQuery(id+"F24.boolean.opBoolean","COPY",EDGE,{"derivedFrom":makeQuery(id+"F24.opExtrude","SWEPT_EDGE",EDGE,{"disambiguationData":[OSD([sQuery(id+"F19.wireOp",EDGE,"E68.bottom"),sQuery(id+"F19.wireOp",EDGE,"E68.right")])]})});
            var Q7;
            Q7=makeQuery(id+"F24.boolean.opBoolean","COPY",EDGE,{"derivedFrom":makeQuery(id+"F24.opExtrude","SWEPT_EDGE",EDGE,{"disambiguationData":[OSD([sQuery(id+"F20.wireOp",EDGE,"E69.bottom"),sQuery(id+"F20.wireOp",EDGE,"E69.right")])]})});
            var Q8;
            Q8=makeQuery(id+"F25.boolean.opBoolean","COPY",EDGE,{"derivedFrom":makeQuery(id+"F25.opExtrude","SWEPT_EDGE",EDGE,{"disambiguationData":[OSD([sQuery(id+"F19.wireOp",EDGE,"E68.top"),sQuery(id+"F19.wireOp",EDGE,"E68.left")])]})});
            var Q9;
            Q9=makeQuery(id+"F25.boolean.opBoolean","COPY",EDGE,{"derivedFrom":makeQuery(id+"F25.opExtrude","SWEPT_EDGE",EDGE,{"disambiguationData":[OSD([sQuery(id+"F19.wireOp",EDGE,"E68.top"),sQuery(id+"F19.wireOp",EDGE,"E68.right")])]})});
            var Q10;
            Q10=makeQuery(id+"F25.boolean.opBoolean","COPY",EDGE,{"derivedFrom":makeQuery(id+"F25.opExtrude","SWEPT_EDGE",EDGE,{"disambiguationData":[OSD([sQuery(id+"F19.wireOp",EDGE,"E68.bottom"),sQuery(id+"F19.wireOp",EDGE,"E68.right")])]})});
            var Q11;
            Q11=makeQuery(id+"F25.boolean.opBoolean","COPY",EDGE,{"derivedFrom":makeQuery(id+"F25.opExtrude","SWEPT_EDGE",EDGE,{"disambiguationData":[OSD([sQuery(id+"F19.wireOp",EDGE,"E68.bottom"),sQuery(id+"F19.wireOp",EDGE,"E68.left")])]})});
            fillet(context, id + "F26", {"entities" : qUnion([Q0, Q1, Q2, Q3, Q4, Q5, Q6, Q7, Q8, Q9, Q10, Q11]), "radius" : 2 * mm, "tangentPropagation" : true, "allowEdgeOverflow" : false});
        }
        {
            var Q0;
            Q0 = qSketchRegion(id + "F22", true);
            extrude(context, id + "F27", {"entities" : qUnion([Q0]), "operationType" : NewBodyOperationType.ADD, "oppositeDirection" : true, "depth" : 2.3 * mm, "offsetDistance" : 25 * mm});
        }
        {
            var Q0;
            {var subQ0=sQuery(id+"F22.wireOp",EDGE,"pXaeYOOe-ctFq-5rke-xXlP-RC25nYOJfYur");var subQ1=sQuery(id+"F22.wireOp",EDGE,"E98");Q0=makeQuery(id+"F27.boolean.opBoolean","MERGE",EDGE,{"derivedFrom":[makeQuery(id+"F23.opExtrude","SWEPT_EDGE",EDGE,{"disambiguationData":[OSD([subQ1,subQ0])]}),makeQuery(id+"F27.opExtrude","SWEPT_EDGE",EDGE,{"disambiguationData":[OSD([subQ1,subQ0])]})]});}
            var Q1;
            Q1=makeQuery(id+"F23.opExtrude","SWEPT_EDGE",EDGE,{"disambiguationData":[OSD([sQuery(id+"F22.wireOp",EDGE,"E77.1"),sQuery(id+"F22.wireOp",EDGE,"E77.3")])]});
            var Q2;
            Q2=makeQuery(id+"F23.opExtrude","SWEPT_EDGE",EDGE,{"disambiguationData":[OSD([sQuery(id+"F22.wireOp",EDGE,"E83.MirrorCS"),sQuery(id+"F22.wireOp",EDGE,"E90.MirrorCS")])]});
            var Q3;
            {var subQ0=sQuery(id+"F22.wireOp",EDGE,"E99");var subQ1=sQuery(id+"F22.wireOp",EDGE,"pXaeYOOe-ctFq-5rke-xXlP-RC25nYOJfYur");Q3=makeQuery(id+"F27.boolean.opBoolean","MERGE",EDGE,{"derivedFrom":[makeQuery(id+"F23.opExtrude","SWEPT_EDGE",EDGE,{"disambiguationData":[OSD([subQ1,subQ0])]}),makeQuery(id+"F27.opExtrude","SWEPT_EDGE",EDGE,{"disambiguationData":[OSD([subQ1,subQ0])]})]});}
            var Q4;
            {var subQ0=sQuery(id+"F22.wireOp",EDGE,"E91.MirrorCS");var subQ1=sQuery(id+"F22.wireOp",EDGE,"E82.MirrorCS");Q4=makeQuery(id+"F27.boolean.opBoolean","MERGE",EDGE,{"derivedFrom":[makeQuery(id+"F23.opExtrude","SWEPT_EDGE",EDGE,{"disambiguationData":[OSD([subQ1,subQ0])]}),makeQuery(id+"F27.opExtrude","SWEPT_EDGE",EDGE,{"disambiguationData":[OSD([subQ1,subQ0])]})]});}
            var Q5;
            {var subQ0=sQuery(id+"F22.wireOp",EDGE,"E72");var subQ1=sQuery(id+"F22.wireOp",EDGE,"E71");Q5=makeQuery(id+"F27.boolean.opBoolean","MERGE",EDGE,{"derivedFrom":[makeQuery(id+"F23.opExtrude","SWEPT_EDGE",EDGE,{"disambiguationData":[OSD([subQ1,subQ0])]}),makeQuery(id+"F27.opExtrude","SWEPT_EDGE",EDGE,{"disambiguationData":[OSD([subQ1,subQ0])]})]});}
            var Q6;
            Q6=makeQuery(id+"F1.opExtrude","SWEPT_EDGE",EDGE,{"disambiguationData":[OSD([sQuery(id+"F0.wireOp",EDGE,"E17"),sQuery(id+"F0.wireOp",EDGE,"E18")])]});
            var Q7;
            Q7=makeQuery(id+"F4.opShell","OFFSET_EDGE",EDGE,{"disambiguationData":[OSD([sQuery(id+"F0.wireOp",EDGE,"E17"),sQuery(id+"F0.wireOp",EDGE,"E18")])]});
            var Q8;
            Q8=makeQuery(id+"F4.opShell","OFFSET_EDGE",EDGE,{"disambiguationData":[OSD([sQuery(id+"F0.wireOp",EDGE,"E20.MirrorCS"),sQuery(id+"F0.wireOp",EDGE,"E21.MirrorCS")])]});
            var Q9;
            Q9=makeQuery(id+"F1.opExtrude","SWEPT_EDGE",EDGE,{"disambiguationData":[OSD([sQuery(id+"F0.wireOp",EDGE,"E20.MirrorCS"),sQuery(id+"F0.wireOp",EDGE,"E21.MirrorCS")])]});
            fillet(context, id + "F28", {"entities" : qUnion([Q0, Q1, Q2, Q3, Q4, Q5, Q6, Q7, Q8, Q9]), "radius" : 5 * mm, "tangentPropagation" : true, "allowEdgeOverflow" : false});
        }
        {
            var Q0;
            {var subQ0=sQuery(id+"F22.wireOp",EDGE,"E96");Q0=makeQuery(id+"F27.boolean.opBoolean","MERGE",FACE,{"derivedFrom":[makeQuery(id+"F1.opExtrude","CAP_FACE",FACE,{"disambiguationData":[OSD([sQuery(id+"F0.wireOp",EDGE,"E0.top"),sQuery(id+"F0.wireOp",EDGE,"E0.right"),sQuery(id+"F0.wireOp",EDGE,"E2.top"),sQuery(id+"F0.wireOp",EDGE,"E2.right"),sQuery(id+"F0.wireOp",EDGE,"E3.MirrorCS"),sQuery(id+"F0.wireOp",EDGE,"E4.MirrorCS"),sQuery(id+"F0.wireOp",EDGE,"E5.MirrorCS"),sQuery(id+"F0.wireOp",EDGE,"E6.MirrorCS"),sQuery(id+"F0.wireOp",EDGE,"E9.trimOffspring"),sQuery(id+"F0.wireOp",EDGE,"E11.trimOffspring"),sQuery(id+"F0.wireOp",EDGE,"E17"),sQuery(id+"F0.wireOp",EDGE,"E18"),sQuery(id+"F0.wireOp",EDGE,"E20.MirrorCS"),sQuery(id+"F0.wireOp",EDGE,"E21.MirrorCS")])],"isStart":true}),makeQuery(id+"F27.opExtrude","CAP_FACE",FACE,{"disambiguationData":[OSD([sQuery(id+"F22.wireOp",EDGE,"E71"),sQuery(id+"F22.wireOp",EDGE,"E72"),sQuery(id+"F22.wireOp",EDGE,"E73"),sQuery(id+"F22.wireOp",EDGE,"E74"),sQuery(id+"F22.wireOp",EDGE,"E75"),sQuery(id+"F22.wireOp",EDGE,"E76"),sQuery(id+"F22.wireOp",EDGE,"E80"),sQuery(id+"F22.wireOp",EDGE,"E81"),sQuery(id+"F22.wireOp",EDGE,"E95"),subQ0,sQuery(id+"F22.wireOp",EDGE,"E98"),sQuery(id+"F22.wireOp",EDGE,"E100"),sQuery(id+"F22.wireOp",EDGE,"E102"),sQuery(id+"F22.wireOp",EDGE,"E103")])],"isStart":false}),makeQuery(id+"F27.opExtrude","CAP_FACE",FACE,{"disambiguationData":[OSD([sQuery(id+"F22.wireOp",EDGE,"E82.MirrorCS"),sQuery(id+"F22.wireOp",EDGE,"E85.MirrorCS"),sQuery(id+"F22.wireOp",EDGE,"E86.MirrorCS"),sQuery(id+"F22.wireOp",EDGE,"E87.MirrorCS"),sQuery(id+"F22.wireOp",EDGE,"E88.MirrorCS"),sQuery(id+"F22.wireOp",EDGE,"E89.MirrorCS"),sQuery(id+"F22.wireOp",EDGE,"E91.MirrorCS"),sQuery(id+"F22.wireOp",EDGE,"E94.MirrorCS"),subQ0,sQuery(id+"F22.wireOp",EDGE,"E97"),sQuery(id+"F22.wireOp",EDGE,"E99"),sQuery(id+"F22.wireOp",EDGE,"E101"),sQuery(id+"F22.wireOp",EDGE,"E104"),sQuery(id+"F22.wireOp",EDGE,"E105")])],"isStart":false})]});}
            var sketch = newSketch(context, id + "F29", { "sketchPlane" : qUnion([Q0])});
            skLineSegment(sketch, "E106.bottom", {"start": v(-91.14, 53.67) * mm, "end": v(91.14, 53.67) * mm});
            skLineSegment(sketch, "E106.top", {"start": v(-91.14, -63.47) * mm, "end": v(91.14, -63.47) * mm});
            skLineSegment(sketch, "E106.left", {"start": v(-91.14, 57.86) * mm, "end": v(-91.14, -63.47) * mm});
            skLineSegment(sketch, "E106.right", {"start": v(91.14, 53.67) * mm, "end": v(91.14, -63.47) * mm});
            skLineSegment(sketch, "E107.bottom", {"start": v(-91.14, 53.67) * mm, "end": v(-75.3, 53.67) * mm});
            skLineSegment(sketch, "E107.top", {"start": v(-91.14, 50.67) * mm, "end": v(-75.3, 50.67) * mm});
            skLineSegment(sketch, "E107.left", {"start": v(-91.14, 53.67) * mm, "end": v(-91.14, 50.67) * mm});
            skLineSegment(sketch, "E107.right", {"start": v(-75.3, 53.67) * mm, "end": v(-75.3, 50.67) * mm});
            skLineSegment(sketch, "E108", {"start": v(0, 53.67) * mm, "end": v(0, 46.16) * mm, "construction": true});
            skLineSegment(sketch, "E109.MirrorCS", {"start": v(75.3, 53.67) * mm, "end": v(75.3, 50.67) * mm});
            skLineSegment(sketch, "E110.MirrorCS", {"start": v(91.14, 50.67) * mm, "end": v(75.3, 50.67) * mm});
            skSolve(sketch);
        }
        {
            var Q0;
            {var subQ0=sQuery(id+"F29.wireOp",EDGE,"E107.right");Q0=makeQuery(id+"F29.imprint","IMPRINT",FACE,{"disambiguationData":[TD([[makeQuery(id+"F29.imprint","IMPRINT",EDGE,{"derivedFrom":subQ0}),1.0]])]});}
            var Q1;
            {var subQ0=sQuery(id+"F29.wireOp",EDGE,"E109.MirrorCS");Q1=makeQuery(id+"F29.imprint","IMPRINT",FACE,{"disambiguationData":[TD([[makeQuery(id+"F29.imprint","IMPRINT",EDGE,{"derivedFrom":subQ0}),-1.0]])]});}
            extrude(context, id + "F30", {"entities" : qUnion([Q0, Q1]), "operationType" : NewBodyOperationType.ADD, "oppositeDirection" : true, "depth" : 102.3 * mm, "offsetDistance" : 25 * mm});
        }
        {
            var Q0;
            {var subQ0=sQuery(id+"F22.wireOp",EDGE,"E102");var subQ1=sQuery(id+"F22.wireOp",EDGE,"E81");Q0=makeQuery(id+"F29.imprint","IMPRINT",FACE,{"disambiguationData":[TD([[makeQuery(id+"F29.imprint","IMPRINT",EDGE,{"derivedFrom":makeQuery(id+"F27.opExtrude","CAP_EDGE",EDGE,{"disambiguationData":[OSD([subQ1,subQ0])],"isStart":false})}),1.0]])]});}
            var Q1;
            {var subQ0=sQuery(id+"F22.wireOp",EDGE,"E104");var subQ4=sQuery(id+"F22.wireOp",EDGE,"E89.MirrorCS");Q1=makeQuery(id+"F29.imprint","IMPRINT",FACE,{"disambiguationData":[TD([[makeQuery(id+"F29.imprint","IMPRINT",EDGE,{"derivedFrom":makeQuery(id+"F27.opExtrude","CAP_EDGE",EDGE,{"disambiguationData":[OSD([subQ4,subQ0])],"isStart":false})}),-1.0]])]});}
            var Q2;
            Q2=makeQuery(id+"F29.imprint","IMPRINT",FACE,{"disambiguationData":[TD([[makeQuery(id+"F29.imprint","IMPRINT",EDGE,{"derivedFrom":makeQuery(id+"F27.opExtrude","CAP_EDGE",EDGE,{"disambiguationData":[OSD([sQuery(id+"F22.wireOp",EDGE,"E86.MirrorCS")])],"isStart":false})}),-1.0]])]});
            var Q3;
            Q3=makeQuery(id+"F29.imprint","IMPRINT",FACE,{"disambiguationData":[TD([[makeQuery(id+"F29.imprint","IMPRINT",EDGE,{"derivedFrom":makeQuery(id+"F27.opExtrude","CAP_EDGE",EDGE,{"disambiguationData":[OSD([sQuery(id+"F22.wireOp",EDGE,"E75")])],"isStart":false})}),1.0]])]});
            extrude(context, id + "F31", {"entities" : qUnion([Q0, Q1, Q2, Q3]), "operationType" : NewBodyOperationType.ADD, "oppositeDirection" : true, "depth" : 2.3 * mm, "offsetDistance" : 25 * mm});
        }
        {
            var Q0;
            Q0=makeQuery(id+"F0.imprint","IMPRINT",FACE,{"disambiguationData":[TD([[makeQuery(id+"F0.imprint","IMPRINT",EDGE,{"derivedFrom":sQuery(id+"F0.wireOp",EDGE,"E32.top")}),-1.0]])]});
            var sketch = newSketch(context, id + "F32", { "sketchPlane" : qUnion([Q0])});
            skLineSegment(sketch, "E111.bottom", {"start": v(-132.34, 8.2) * mm, "end": v(-317.54, 8.2) * mm});
            skLineSegment(sketch, "E111.top", {"start": v(-132.34, 98.5) * mm, "end": v(-137.54, 98.5) * mm});
            skLineSegment(sketch, "E111.left", {"start": v(-132.34, 8.2) * mm, "end": v(-132.34, 98.5) * mm});
            skLineSegment(sketch, "E111.right", {"start": v(-317.54, 8.2) * mm, "end": v(-317.54, 98.5) * mm});
            skLineSegment(sketch, "E112.top", {"start": v(-137.54, 104.5) * mm, "end": v(-149.34, 104.5) * mm});
            skLineSegment(sketch, "E112.left", {"start": v(-137.54, 98.5) * mm, "end": v(-137.54, 104.5) * mm});
            skLineSegment(sketch, "E112.right", {"start": v(-149.34, 98.5) * mm, "end": v(-149.34, 104.5) * mm});
            skLineSegment(sketch, "E113.MirrorCS", {"start": v(-300.54, 98.5) * mm, "end": v(-300.54, 104.5) * mm});
            skLineSegment(sketch, "E114.trimOffspring", {"start": v(-149.34, 98.5) * mm, "end": v(-300.54, 98.5) * mm});
            skLineSegment(sketch, "E115", {"start": v(-300.54, 104.5) * mm, "end": v(-315.24, 104.5) * mm});
            skLineSegment(sketch, "E116", {"start": v(-315.24, 104.5) * mm, "end": v(-315.24, 98.5) * mm});
            skLineSegment(sketch, "E117", {"start": v(-315.24, 98.5) * mm, "end": v(-317.54, 98.5) * mm});
            skSolve(sketch);
        }
        {
            var Q0;
            Q0=makeQuery(id+"F32.imprint","IMPRINT",FACE,{"disambiguationData":[TD([[makeQuery(id+"F32.imprint","IMPRINT",EDGE,{"derivedFrom":sQuery(id+"F32.wireOp",EDGE,"E111.bottom")}),1.0]])]});
            var Q1;
            {var subQ4=sQuery(id+"F32.wireOp",EDGE,"E114.trimOffspring");Q1=makeQuery(id+"F32.imprint","IMPRINT",FACE,{"disambiguationData":[TD([[makeQuery(id+"F32.imprint","IMPRINT",EDGE,{"derivedFrom":subQ4}),1.0]])]});}
            var Q2;
            Q2=makeQuery(id+"F0.imprint","IMPRINT",FACE,{"disambiguationData":[TD([[makeQuery(id+"F0.imprint","IMPRINT",EDGE,{"derivedFrom":sQuery(id+"F0.wireOp",EDGE,"E32.top")}),-1.0]])]});
            extrude(context, id + "F33", {"entities" : qUnion([Q0, Q1, Q2]), "operationType" : NewBodyOperationType.ADD, "oppositeDirection" : true, "depth" : 2.3 * mm, "offsetDistance" : 25 * mm});
        }
        {
            var Q0;
            {var subQ0=sQuery(id+"F0.wireOp",EDGE,"E42");var subQ1=sQuery(id+"F0.wireOp",EDGE,"E36.5");Q0=makeQuery(id+"F33.boolean.opBoolean","MERGE",EDGE,{"derivedFrom":[makeQuery(id+"F2.opExtrude","SWEPT_EDGE",EDGE,{"disambiguationData":[OSD([subQ1,subQ0])]}),makeQuery(id+"F33.opExtrude","SWEPT_EDGE",EDGE,{"disambiguationData":[OSD([subQ1,subQ0])]})]});}
            var Q1;
            Q1=makeQuery(id+"F1.opExtrude","SWEPT_EDGE",EDGE,{"disambiguationData":[OSD([sQuery(id+"F0.wireOp",EDGE,"E32.right"),sQuery(id+"F0.wireOp",EDGE,"E41")])]});
            var Q2;
            {var subQ0=sQuery(id+"F0.wireOp",EDGE,"E42");var subQ1=sQuery(id+"F0.wireOp",EDGE,"E36.1");Q2=makeQuery(id+"F33.boolean.opBoolean","MERGE",EDGE,{"derivedFrom":[makeQuery(id+"F2.opExtrude","SWEPT_EDGE",EDGE,{"disambiguationData":[OSD([subQ1,subQ0])]}),makeQuery(id+"F33.opExtrude","SWEPT_EDGE",EDGE,{"disambiguationData":[OSD([subQ1,subQ0])]})]});}
            var Q3;
            Q3=makeQuery(id+"F1.opExtrude","SWEPT_EDGE",EDGE,{"disambiguationData":[OSD([sQuery(id+"F0.wireOp",EDGE,"E33.MirrorCS"),sQuery(id+"F0.wireOp",EDGE,"E41")])]});
            var Q4;
            Q4=makeQuery(id+"F1.opExtrude","SWEPT_EDGE",EDGE,{"disambiguationData":[OSD([sQuery(id+"F0.wireOp",EDGE,"E33.MirrorCS"),sQuery(id+"F0.wireOp",EDGE,"E50.MirrorCS")])]});
            var Q5;
            Q5=makeQuery(id+"F1.opExtrude","SWEPT_EDGE",EDGE,{"disambiguationData":[OSD([sQuery(id+"F0.wireOp",EDGE,"E32.top"),sQuery(id+"F0.wireOp",EDGE,"E32.right")])]});
            fillet(context, id + "F34", {"entities" : qUnion([Q0, Q1, Q2, Q3, Q4, Q5]), "radius" : 5 * mm, "tangentPropagation" : true, "allowEdgeOverflow" : false});
        }
        {
            var Q0;
            Q0=makeQuery(id+"F2.opExtrude","SWEPT_EDGE",EDGE,{"disambiguationData":[OSD([sQuery(id+"F0.wireOp",EDGE,"E32.right"),sQuery(id+"F0.wireOp",EDGE,"E41")])]});
            var Q1;
            Q1=makeQuery(id+"F2.opExtrude","SWEPT_EDGE",EDGE,{"disambiguationData":[OSD([sQuery(id+"F0.wireOp",EDGE,"E33.MirrorCS"),sQuery(id+"F0.wireOp",EDGE,"E41")])]});
            fillet(context, id + "F35", {"entities" : qUnion([Q0, Q1]), "radius" : 2 * mm, "tangentPropagation" : true, "allowEdgeOverflow" : false});
        }
        {
            var Q0;
            {var subQ0=sQuery(id+"F0.wireOp",EDGE,"E53");var subQ1=sQuery(id+"F0.wireOp",EDGE,"E52");var subQ2=sQuery(id+"F0.wireOp",EDGE,"E46.MirrorCS");Q0=makeQuery(id+"F33.boolean.opBoolean","MERGE",FACE,{"derivedFrom":[makeQuery(id+"F33.opExtrude","CAP_FACE",FACE,{"disambiguationData":[OSD([sQuery(id+"F0.wireOp",EDGE,"E32.top"),sQuery(id+"F0.wireOp",EDGE,"E32.right"),sQuery(id+"F0.wireOp",EDGE,"E33.MirrorCS"),sQuery(id+"F0.wireOp",EDGE,"E36.1"),sQuery(id+"F0.wireOp",EDGE,"E36.4"),sQuery(id+"F0.wireOp",EDGE,"E36.5"),sQuery(id+"F0.wireOp",EDGE,"E37"),sQuery(id+"F0.wireOp",EDGE,"E38.top"),sQuery(id+"F0.wireOp",EDGE,"E38.right"),sQuery(id+"F0.wireOp",EDGE,"E39.bottom"),sQuery(id+"F0.wireOp",EDGE,"E39.top"),sQuery(id+"F0.wireOp",EDGE,"E39.right"),sQuery(id+"F0.wireOp",EDGE,"E40.trimOffspring"),sQuery(id+"F0.wireOp",EDGE,"E41"),sQuery(id+"F0.wireOp",EDGE,"E42"),sQuery(id+"F0.wireOp",EDGE,"E44.MirrorCS"),sQuery(id+"F0.wireOp",EDGE,"E45.MirrorCS"),subQ2,sQuery(id+"F0.wireOp",EDGE,"E47.MirrorCS"),sQuery(id+"F0.wireOp",EDGE,"E48.MirrorCS"),sQuery(id+"F0.wireOp",EDGE,"E49.MirrorCS"),sQuery(id+"F0.wireOp",EDGE,"E50.MirrorCS"),sQuery(id+"F0.wireOp",EDGE,"E51.MirrorCS"),subQ1,subQ0,sQuery(id+"F0.wireOp",EDGE,"E55.MirrorCS"),sQuery(id+"F0.wireOp",EDGE,"E56.MirrorCS"),sQuery(id+"F0.wireOp",EDGE,"E57.MirrorCS")])],"isStart":false}),makeQuery(id+"F33.opExtrude","CAP_FACE",FACE,{"disambiguationData":[OSD([subQ2,subQ1,subQ0,sQuery(id+"F32.wireOp",EDGE,"E111.bottom"),sQuery(id+"F32.wireOp",EDGE,"E111.top"),sQuery(id+"F32.wireOp",EDGE,"E111.left"),sQuery(id+"F32.wireOp",EDGE,"E111.right"),sQuery(id+"F32.wireOp",EDGE,"E112.left"),sQuery(id+"F32.wireOp",EDGE,"E112.right"),sQuery(id+"F32.wireOp",EDGE,"E113.MirrorCS"),sQuery(id+"F32.wireOp",EDGE,"E114.trimOffspring"),sQuery(id+"F32.wireOp",EDGE,"E115"),sQuery(id+"F32.wireOp",EDGE,"E117")])],"isStart":false})]});}
            var sketch = newSketch(context, id + "F36", { "sketchPlane" : qUnion([Q0])});
            skLineSegment(sketch, "E118.bottom", {"start": v(-149.34, -98.5) * mm, "end": v(-300.54, -98.5) * mm});
            skLineSegment(sketch, "E118.top", {"start": v(-149.34, -104.5) * mm, "end": v(-300.54, -104.5) * mm});
            skLineSegment(sketch, "E118.left", {"start": v(-149.34, -98.5) * mm, "end": v(-149.34, -104.5) * mm});
            skLineSegment(sketch, "E118.right", {"start": v(-300.54, -98.5) * mm, "end": v(-300.54, -104.5) * mm});
            skSolve(sketch);
        }
        {
            var Q0;
            Q0=makeQuery(id+"F36.imprint","IMPRINT",FACE,{"disambiguationData":[TD([[makeQuery(id+"F36.imprint","IMPRINT",EDGE,{"derivedFrom":sQuery(id+"F36.wireOp",EDGE,"E118.bottom")}),1.0]])]});
            extrude(context, id + "F37", {"entities" : qUnion([Q0]), "operationType" : NewBodyOperationType.ADD, "oppositeDirection" : true, "depth" : 1.15 * mm, "offsetDistance" : 25 * mm});
        }
        {
            var Q0;
            {var subQ0=sQuery(id+"F0.wireOp",EDGE,"E6.MirrorCS");var subQ3=sQuery(id+"F0.wireOp",EDGE,"E0.top");Q0=makeQuery(id+"F29.imprint","IMPRINT",FACE,{"disambiguationData":[TD([[makeQuery(id+"F29.imprint","IMPRINT",EDGE,{"derivedFrom":makeQuery(id+"F1.opExtrude","CAP_EDGE",EDGE,{"disambiguationData":[OSD([subQ3,subQ0])],"isStart":true})}),1.0]])]});}
            extrude(context, id + "F38", {"entities" : qUnion([Q0]), "operationType" : NewBodyOperationType.REMOVE, "oppositeDirection" : true, "depth" : 1.15 * mm, "offsetDistance" : 25 * mm});
        }
        {
            var Q0;
            {var subQ0=sQuery(id+"F0.wireOp",EDGE,"E53");var subQ1=sQuery(id+"F0.wireOp",EDGE,"E52");var subQ2=sQuery(id+"F0.wireOp",EDGE,"E46.MirrorCS");Q0=makeQuery(id+"F33.boolean.opBoolean","MERGE",FACE,{"derivedFrom":[makeQuery(id+"F33.opExtrude","CAP_FACE",FACE,{"disambiguationData":[OSD([sQuery(id+"F0.wireOp",EDGE,"E32.top"),sQuery(id+"F0.wireOp",EDGE,"E32.right"),sQuery(id+"F0.wireOp",EDGE,"E33.MirrorCS"),sQuery(id+"F0.wireOp",EDGE,"E36.1"),sQuery(id+"F0.wireOp",EDGE,"E36.4"),sQuery(id+"F0.wireOp",EDGE,"E36.5"),sQuery(id+"F0.wireOp",EDGE,"E37"),sQuery(id+"F0.wireOp",EDGE,"E38.top"),sQuery(id+"F0.wireOp",EDGE,"E38.right"),sQuery(id+"F0.wireOp",EDGE,"E39.bottom"),sQuery(id+"F0.wireOp",EDGE,"E39.top"),sQuery(id+"F0.wireOp",EDGE,"E39.right"),sQuery(id+"F0.wireOp",EDGE,"E40.trimOffspring"),sQuery(id+"F0.wireOp",EDGE,"E41"),sQuery(id+"F0.wireOp",EDGE,"E42"),sQuery(id+"F0.wireOp",EDGE,"E44.MirrorCS"),sQuery(id+"F0.wireOp",EDGE,"E45.MirrorCS"),subQ2,sQuery(id+"F0.wireOp",EDGE,"E47.MirrorCS"),sQuery(id+"F0.wireOp",EDGE,"E48.MirrorCS"),sQuery(id+"F0.wireOp",EDGE,"E49.MirrorCS"),sQuery(id+"F0.wireOp",EDGE,"E50.MirrorCS"),sQuery(id+"F0.wireOp",EDGE,"E51.MirrorCS"),subQ1,subQ0,sQuery(id+"F0.wireOp",EDGE,"E55.MirrorCS"),sQuery(id+"F0.wireOp",EDGE,"E56.MirrorCS"),sQuery(id+"F0.wireOp",EDGE,"E57.MirrorCS")])],"isStart":true}),makeQuery(id+"F33.opExtrude","CAP_FACE",FACE,{"disambiguationData":[OSD([subQ2,subQ1,subQ0,sQuery(id+"F32.wireOp",EDGE,"E111.bottom"),sQuery(id+"F32.wireOp",EDGE,"E111.top"),sQuery(id+"F32.wireOp",EDGE,"E111.left"),sQuery(id+"F32.wireOp",EDGE,"E111.right"),sQuery(id+"F32.wireOp",EDGE,"E112.left"),sQuery(id+"F32.wireOp",EDGE,"E112.right"),sQuery(id+"F32.wireOp",EDGE,"E113.MirrorCS"),sQuery(id+"F32.wireOp",EDGE,"E114.trimOffspring"),sQuery(id+"F32.wireOp",EDGE,"E115"),sQuery(id+"F32.wireOp",EDGE,"E117")])],"isStart":true})]});}
            var sketch = newSketch(context, id + "F39", { "sketchPlane" : qUnion([Q0])});
            skText(sketch, "E119", { "text": "The Great\n Magician", "fontName": "OpenSans-Bold.ttf"});
            const initialGuessF39  = {"E119": [-0.28491, 0.06366, 1, 0, 0.01754]};
            skSetInitialGuess(sketch, initialGuessF39);
            skSolve(sketch);
        }
        {
            var Q0;
            Q0 = qSketchRegion(id + "F39", true);
            extrude(context, id + "F40", {"entities" : qUnion([Q0]), "operationType" : NewBodyOperationType.REMOVE, "oppositeDirection" : true, "depth" : .2 * mm, "offsetDistance" : 25 * mm});
        }
        {
            var Q0;
            Q0=makeQuery(id+"F7.opExtrude","CAP_FACE",FACE,{"disambiguationData":[OSD([sQuery(id+"F0.wireOp",EDGE,"E16"),sQuery(id+"F0.wireOp",EDGE,"E23"),sQuery(id+"F0.wireOp",EDGE,"E24"),sQuery(id+"F0.wireOp",EDGE,"E25.MirrorCS"),sQuery(id+"F0.wireOp",EDGE,"E26.MirrorCS"),sQuery(id+"F0.wireOp",EDGE,"E29"),sQuery(id+"F0.wireOp",EDGE,"E30"),sQuery(id+"F0.wireOp",EDGE,"E31")])],"isStart":false});
            var sketch = newSketch(context, id + "F41", { "sketchPlane" : qUnion([Q0])});
            skLineSegment(sketch, "E120", {"start": v(-33.7, 25.33) * mm, "end": v(-33.7, -3.3) * mm});
            skLineSegment(sketch, "E121", {"start": v(-33.7, -3.3) * mm, "end": v(0, -3.3) * mm});
            skLineSegment(sketch, "E122", {"start": v(-33.7, 25.33) * mm, "end": v(-28.06, 25.33) * mm});
            skLineSegment(sketch, "E123", {"start": v(-28.06, 25.33) * mm, "end": v(-21.56, 9.02) * mm});
            skLineSegment(sketch, "E124", {"start": v(-21.56, 9.02) * mm, "end": v(0, 9.02) * mm});
            skLineSegment(sketch, "E125", {"start": v(0, 9.02) * mm, "end": v(0, -3.3) * mm, "construction": true});
            skLineSegment(sketch, "E126.MirrorCS", {"start": v(21.56, 9.02) * mm, "end": v(0, 9.02) * mm});
            skLineSegment(sketch, "E127.MirrorCS", {"start": v(28.06, 25.33) * mm, "end": v(21.56, 9.02) * mm});
            skLineSegment(sketch, "E128.MirrorCS", {"start": v(33.7, 25.33) * mm, "end": v(28.06, 25.33) * mm});
            skLineSegment(sketch, "E129.MirrorCS", {"start": v(33.7, 25.33) * mm, "end": v(33.7, -3.3) * mm});
            skLineSegment(sketch, "E130.MirrorCS", {"start": v(33.7, -3.3) * mm, "end": v(0, -3.3) * mm});
            skSolve(sketch);
        }
        {
            var Q0;
            Q0 = qSketchRegion(id + "F41", true);
            extrude(context, id + "F42", {"entities" : qUnion([Q0]), "operationType" : NewBodyOperationType.REMOVE, "oppositeDirection" : true, "depth" : 33 * mm, "offsetDistance" : 25 * mm});
        }
    });
